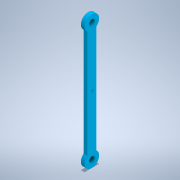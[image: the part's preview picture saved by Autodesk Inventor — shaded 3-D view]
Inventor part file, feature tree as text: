
AUTODESK INVENTOR PART (.ipt)
format: ipt  version: 2020 (Build 240168000, 168)  size: 121,856 bytes
history: native  units: in
note: dims shown in document units (in); Inventor stores cm internally (conversion verified against a paired STEP export)
features: extrude x1, sketch x1
ambient origin geometry x8: Origin, YZ Plane, XZ Plane, XY Plane, X Axis, Y Axis, Z Axis, Center Point
bodies: Solid1 (feature_tree)
feature tree (2):
  extrude  "Extrusion1"  Depth=1.9685in
  sketch  "Sketch1"  dims[d0=23.622in d1=1.9685in d2=0.9843in d3=11.811in d4=1.1811in d5=0.9843in d6=3.1496in d11=0.3937in d12=0.7874in d13=0.0in d14=0.0in d15=1.1811in d16=3.1496in d17=0.9843in]
